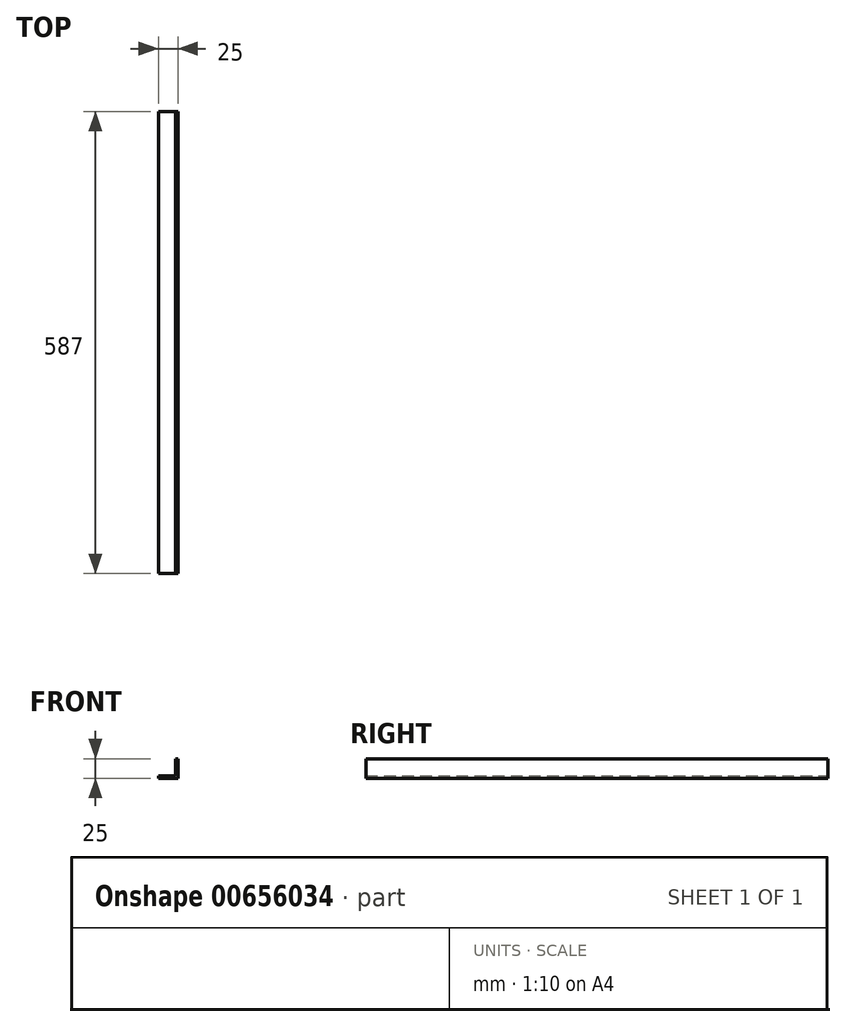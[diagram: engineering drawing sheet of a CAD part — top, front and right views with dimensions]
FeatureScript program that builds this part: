
annotation { "Feature Type Name" : "Feature", "Feature Type Description" : "" }
export const myFeature = defineFeature(function(context is Context, id is Id, definition is map)
    precondition{}
    {
        {
            var Q0;
            Q0=qCreatedBy(makeId("Front.planeOp"),FACE);
            var sketch = newSketch(context, id + "F0", { "sketchPlane" : qUnion([Q0])});
            skLineSegment(sketch, "E0", {"start": v(0, 0) * mm, "end": v(0, 22) * mm});
            skLineSegment(sketch, "E1", {"start": v(0, 22) * mm, "end": v(3, 22) * mm});
            skLineSegment(sketch, "E2", {"start": v(3, 22) * mm, "end": v(3, -3) * mm});
            skLineSegment(sketch, "E3", {"start": v(3, -3) * mm, "end": v(-22, -3) * mm});
            skLineSegment(sketch, "E4", {"start": v(-22, -3) * mm, "end": v(-22, 0) * mm});
            skLineSegment(sketch, "E5", {"start": v(-22, 0) * mm, "end": v(0, 0) * mm});
            skSolve(sketch);
        }
        {
            var Q0;
            Q0=makeQuery(id+"F0.imprint","IMPRINT",FACE,{"disambiguationData":[TD([[makeQuery(id+"F0.imprint","IMPRINT",EDGE,{"derivedFrom":sQuery(id+"F0.wireOp",EDGE,"E0")}),-1.0]])]});
            extrude(context, id + "F1", {"entities" : qUnion([Q0]), "depth" : 587 * mm, "offsetDistance" : 25.4 * mm});
        }
    });
